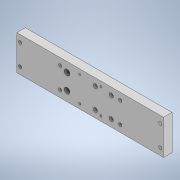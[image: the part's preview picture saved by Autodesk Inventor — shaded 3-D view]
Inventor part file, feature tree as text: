
AUTODESK INVENTOR PART (.ipt)
format: ipt  version: 2020 (Build 240168000, 168)  size: 253,952 bytes
history: native  units: in
note: dims shown in document units (in); Inventor stores cm internally (conversion verified against a paired STEP export)
features: sketch x9, extrude x6, other x4, reference x2, fillet x1
ambient origin geometry x8: Origin, YZ Plane, XZ Plane, XY Plane, X Axis, Y Axis, Z Axis, Center Point
bodies: Solid1 (feature_tree)
feature tree (22):
  extrude  "Extrusion1"  Depth=0.5in
  extrude  "Extrusion2"  Depth=0.1181in
  extrude  "Extrusion3"  Depth=0.5in TaperAngle=0.0deg
  sketch  "Sketch5"  dims[d11=0.7874in d13=0.9449in d14=0.7874in d16=1.2205in d19=0.5in d20=0.0in]
  sketch  "Sketch6"  dims[d21=0.25in d22=0.25in]
  sketch  "Sketch7"  dims[d23=0.25in d24=0.25in]
  extrude  "Extrusion4"  Depth=0.25in
  extrude  "Extrusion5"  Depth=0.25in
  extrude  "Extrusion6"  Depth=0.125in
  fillet  "Fillet1"  Radius=0.6125in
  sketch  "Sketch11"  dims[d38=1.0in d39=0.0in d40=0.25in d41=0.25in d42=0.25in d43=0.25in d44=0.125in d45=0.0in d46=0.3125in d47=0.3125in d48=0.5in d49=0.0in d50=0.01in d51=0.4062in d53=0.1875in d54=8.6875in d55=0.1875in d56=2.5625in d57=3.7313in d58=4.6489in d59=0.3125in d60=4.9813in d61=5.5938in d62=6.125in d63=8.5in d64=0.5698in d65=1.6563in d66=0.2812in d67=1.5048in d68=0.421in d69=1.7812in d70=1.6415in d71=2.0625in]
  sketch  "Sketch3"  dims[d0=0.5in d1=0.0in d8=0.6102in]
  sketch  "Sketch4"  dims[d9=1.25in d10=0.1181in]
  sketch  "Sketch8"  dims[d25=0.125in d26=0.0in d27=0.125in d28=0.6125in]
  sketch  "Sketch9"  dims[d29=0.7874in d31=1.5in d32=0.7874in d34=1.25in]
  sketch  "Sketch10"  dims[d37=0.75in]
  reference  "Reference11"
  reference  "Reference12"
  other  "<userpath>\Desktop\PnP Machine\PnP Machine.iam"
  other  "PnP Machine.iam"
  other  "5779K109_PUSH-TO-CONNECT TUBE FITTING FOR AIR:1"
  other  "5779K109_PUSH-TO-CONNECT TUBE FITTING FOR AIR:2"
